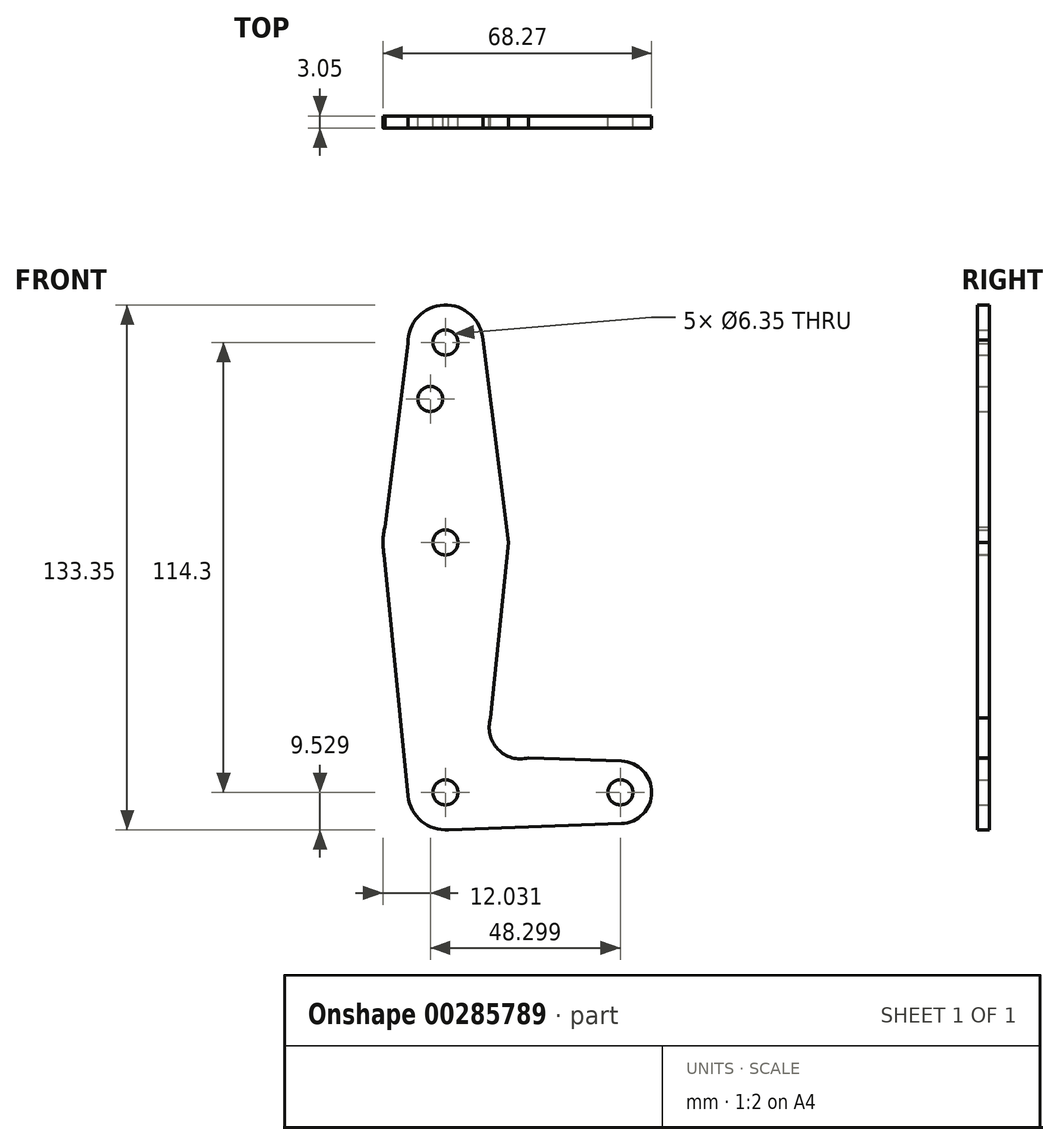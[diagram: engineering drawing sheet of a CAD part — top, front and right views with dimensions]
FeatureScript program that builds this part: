
annotation { "Feature Type Name" : "Feature", "Feature Type Description" : "" }
export const myFeature = defineFeature(function(context is Context, id is Id, definition is map)
    precondition{}
    {
        {
            var Q0;
            Q0=qCreatedBy(makeId("Front.planeOp"),FACE);
            var sketch = newSketch(context, id + "F0", { "sketchPlane" : qUnion([Q0])});
            skLineSegment(sketch, "E0", {"start": v(-44.45, 38.1) * mm, "end": v(-44.45, -76.2) * mm});
            skCircle(sketch, "E1", {"center": v(-44.45, -76.2) * mm, "radius": 9.53 * mm});
            skCircle(sketch, "E2", {"center": v(0, -76.2) * mm, "radius": 7.94 * mm});
            skCircle(sketch, "E3", {"center": v(-44.45, 38.1) * mm, "radius": 9.53 * mm});
            skCircle(sketch, "E4", {"center": v(-44.45, -12.7) * mm, "radius": 15.88 * mm});
            skLineSegment(sketch, "E5", {"start": v(-53.97, 37.89) * mm, "end": v(-60.32, -12.77) * mm});
            skLineSegment(sketch, "E6", {"start": v(-60.32, -12.77) * mm, "end": v(-53.93, -77.14) * mm});
            skLineSegment(sketch, "E7", {"start": v(-34.94, 38.7) * mm, "end": v(-28.44, -12.77) * mm});
            skArc(sketch, "E8", {"start": v(-32.96, -57.32) * mm, "mid": v(-31.15, -65.23) * mm, "end": v(-23.34, -67.43) * mm});
            skLineSegment(sketch, "E9", {"start": v(-44.45, -12.7) * mm, "end": v(-44.45, -76.2) * mm});
            skCircle(sketch, "E10", {"center": v(-44.45, -76.2) * mm, "radius": 3.18 * mm});
            skCircle(sketch, "E11", {"center": v(0, -76.2) * mm, "radius": 3.18 * mm});
            skCircle(sketch, "E12", {"center": v(-44.45, 38.1) * mm, "radius": 3.18 * mm});
            skCircle(sketch, "E13", {"center": v(-44.45, -12.7) * mm, "radius": 3.18 * mm});
            skLineSegment(sketch, "E14", {"start": v(-28.44, -12.77) * mm, "end": v(-32.96, -57.32) * mm});
            skLineSegment(sketch, "E15", {"start": v(-44.45, -76.2) * mm, "end": v(0, -76.2) * mm});
            skLineSegment(sketch, "E16", {"start": v(-23.34, -67.43) * mm, "end": v(0.28, -68.27) * mm});
            skLineSegment(sketch, "E17", {"start": v(-44.58, -85.73) * mm, "end": v(0.28, -84.13) * mm});
            skLineSegment(sketch, "E18", {"start": v(-44.45, -76.2) * mm, "end": v(-34.93, -76.2) * mm});
            skLineSegment(sketch, "E19", {"start": v(-44.45, -76.2) * mm, "end": v(-44.45, -66.68) * mm});
            skCircle(sketch, "E20", {"center": v(-48.3, 23.75) * mm, "radius": 3.18 * mm});
            skSolve(sketch);
        }
        {
            var Q0;
            Q0=sQuery(id+"F0.wireOp",EDGE,"E14");
            extrude(context, id + "F1", {"bodyType" : ToolBodyType.SURFACE, "surfaceEntities" : qUnion([Q0]), "depth" : 3.05 * mm});
        }
        {
            var Q0;
            Q0 = qSketchRegion(id + "F0", true);
            extrude(context, id + "F2", {"entities" : qUnion([Q0]), "depth" : 3.05 * mm});
        }
        {
            var Q0;
            Q0=sQuery(id+"F0.wireOp",EDGE,"E8");
            extrude(context, id + "F3", {"bodyType" : ToolBodyType.SURFACE, "surfaceEntities" : qUnion([Q0]), "depth" : 3.05 * mm});
        }
        {
            var Q0;
            {var subQ3=sQuery(id+"F0.wireOp",EDGE,"E18");var subQ5=sQuery(id+"F0.wireOp",EDGE,"E10");var subQ6=makeQuery(id+"F0.imprint","INTERSECT",VERTEX,{"derivedFrom":[subQ5,subQ3]});Q0=makeQuery(id+"F0.imprint","IMPRINT",FACE,{"disambiguationData":[TD([[makeQuery(id+"F0.imprint","IMPRINT",EDGE,{"disambiguationData":[TD([[subQ6,-1.0]])],"derivedFrom":subQ5}),-1.0]])]});}
            extrude(context, id + "F4", {"entities" : qUnion([Q0]), "operationType" : NewBodyOperationType.ADD, "depth" : 3.05 * mm});
        }
    });
